# Revit family: Scale-SR_Scales-SRV947IFS
name_source: partatom
category: Specialty Equipment
units: mm (PartAtom-declared; Revit-internal decimal feet)

## family parameters
Always vertical = Yes
Cut with Voids When Loaded = No
Host = Floor
Part Type = Normal
Room Calculation Point = No
Round Connector Dimension = Use Diameter
Shared = No

## types (1)
- SRV947IFS
    Accuracy = 0.2% +/- 1 Digits of Displayed Resolution
    Assembly Code = E1020810
    Auto Zero = One Button Operation / Hold for Zero
    Averaging = Automatic Digital Filter
    BIM Version = v4.1
    BIM Version Available (Earliest) = Revit 2020
    Button Functions = On/Off, Weigh, Unit and Hold
    Calibration = Traceable to NIST Standards
    Default Elevation = 0"
    Description = 24" x 48" In-Floor Scale with Wall Display
    Display Resolution = 0.2 lb / 0.1 kg
    Display Type = 1'' Digit LCD
    Display Units = Pounds / Kilograms
    Manufacturer = SR Scales by SR Instruments, Inc.
    Maximum Weight Capacity = 400 lbs or 182 kg
    Memory Recall = Recalls Last Stored Weight
    Model = SRV947IFS
    Platform Size = 24'' x 48'' x 2'' (61 cm x 122 cm x 5 cm)
    Power Supply = 110v AC, 50-60 Hz
    Product Brochure Link = https://srinstruments.com
    Product Page URL = https://srinstruments.com
    URL = http://www.srinstruments.com

## geometry (parser evidence)
native form markers: Blend x1, Sweep x5
no freeform markers — native parametric forms only
